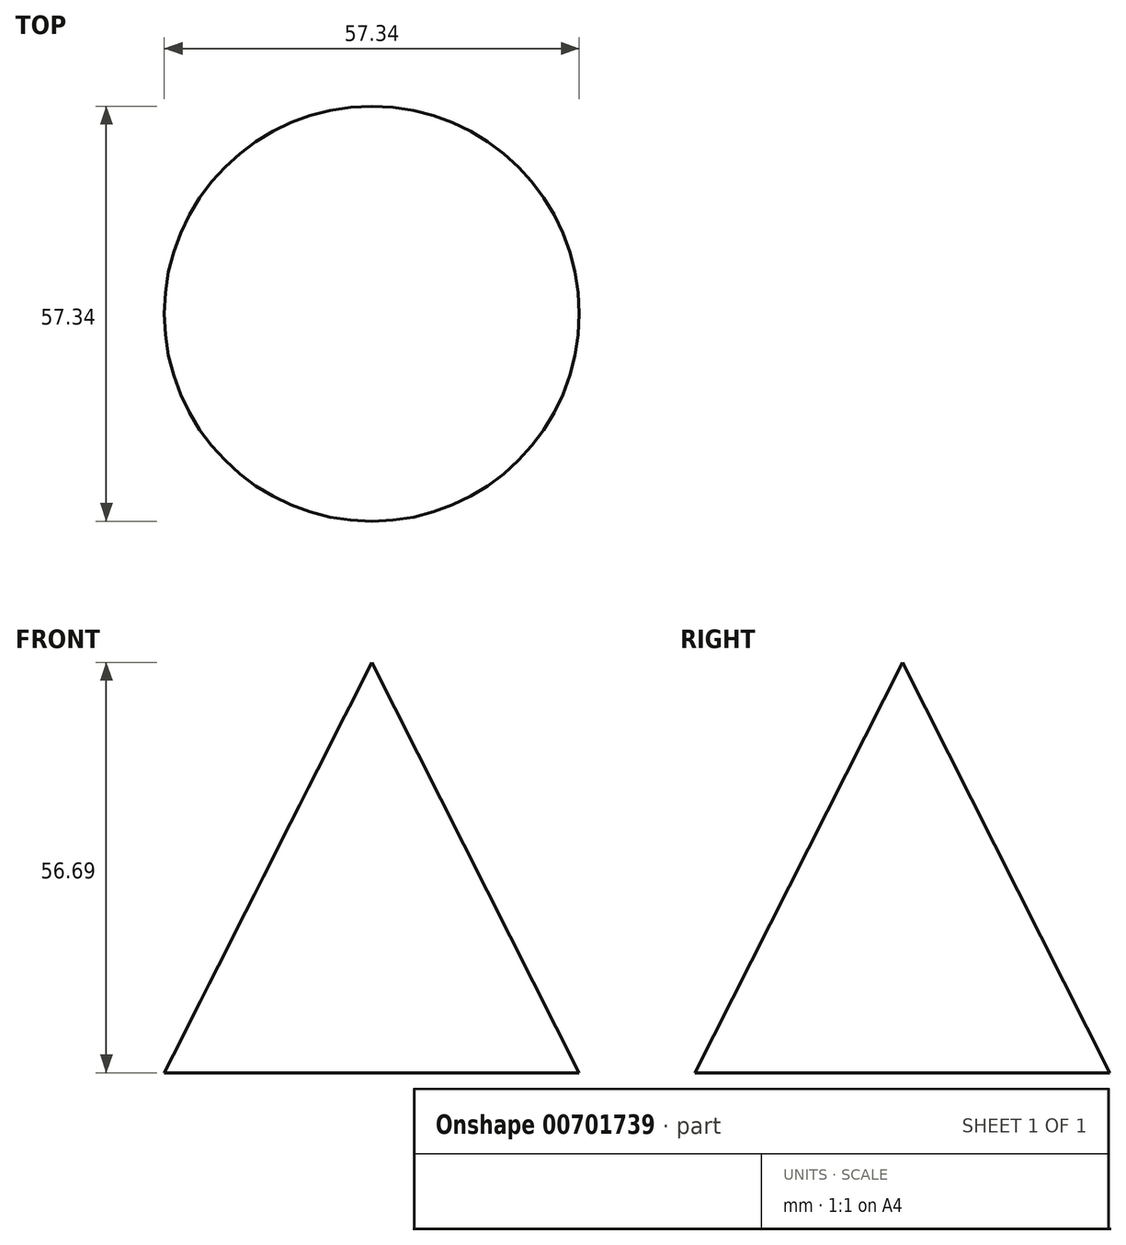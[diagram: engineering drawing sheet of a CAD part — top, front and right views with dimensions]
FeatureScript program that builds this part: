
annotation { "Feature Type Name" : "Feature", "Feature Type Description" : "" }
export const myFeature = defineFeature(function(context is Context, id is Id, definition is map)
    precondition{}
    {
        {
            var Q0;
            Q0=qCreatedBy(makeId("Front.planeOp"),FACE);
            var sketch = newSketch(context, id + "F0", { "sketchPlane" : qUnion([Q0])});
            skLineSegment(sketch, "E0", {"start": v(-28.67, 0) * mm, "end": v(0, 56.69) * mm});
            skLineSegment(sketch, "E1", {"start": v(0, 0) * mm, "end": v(-28.67, 0) * mm});
            skLineSegment(sketch, "E2", {"start": v(0, 56.69) * mm, "end": v(0, 0) * mm});
            skSolve(sketch);
        }
        {
            var Q0;
            Q0=sQuery(id+"F0.wireOp",EDGE,"E0");
            var Q1;
            Q1=sQuery(id+"F0.wireOp",EDGE,"E1");
            var Q2;
            Q2=sQuery(id+"F0.wireOp",EDGE,"E2");
            revolve(context, id + "F1", {"bodyType" : ToolBodyType.SURFACE, "surfaceOperationType" : NewSurfaceOperationType.NEW, "surfaceEntities" : qUnion([Q0, Q1]), "axis" : qUnion([Q2]), "revolveType" : RevolveType.FULL});
        }
    });
